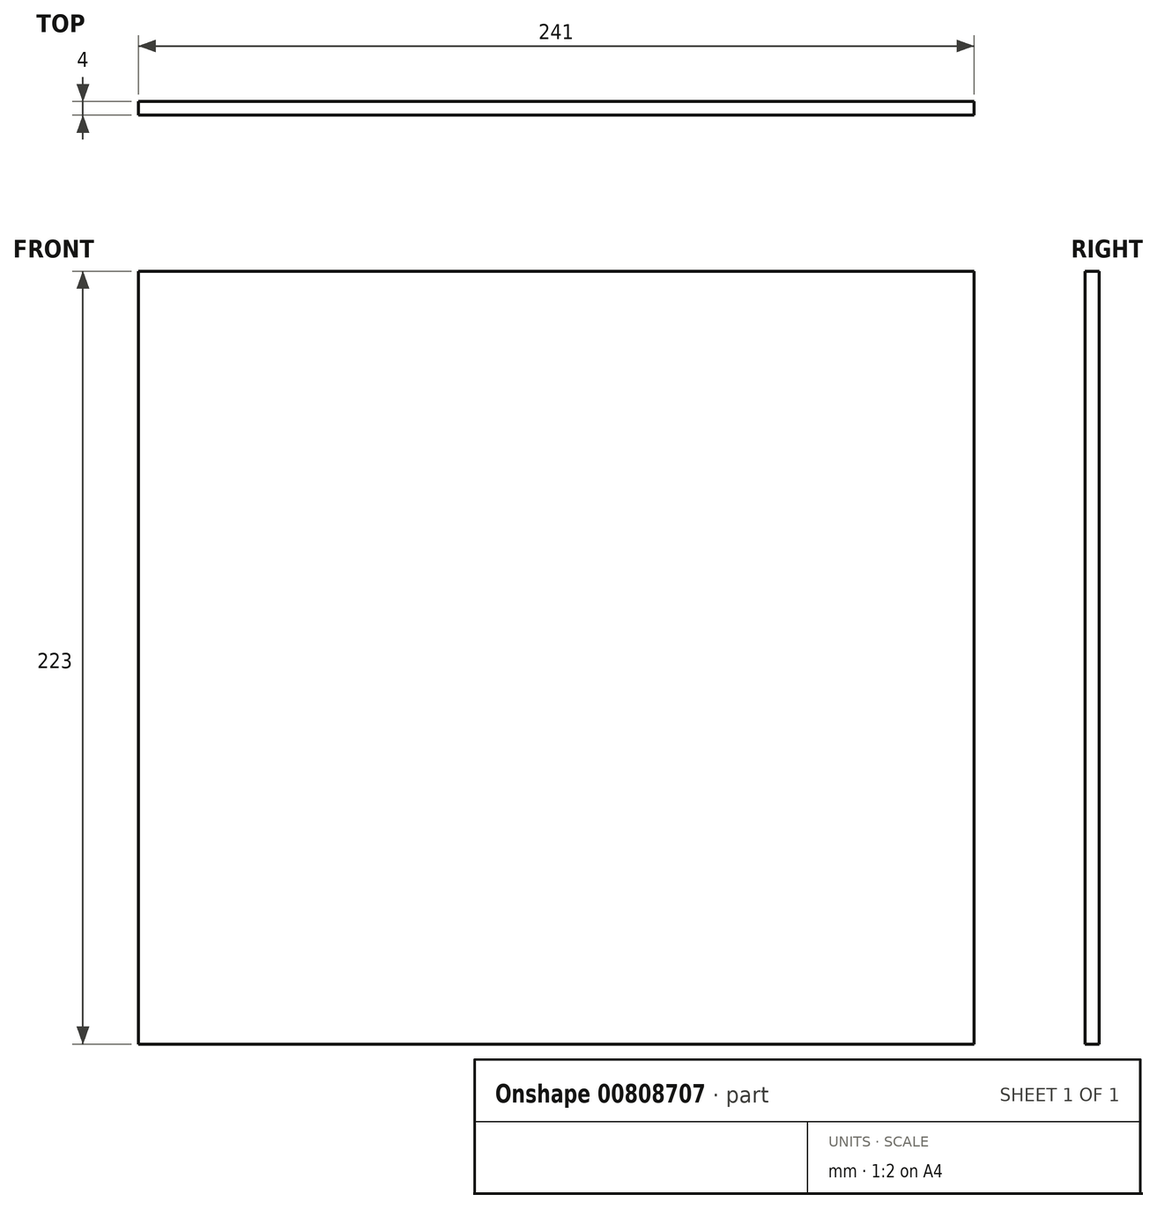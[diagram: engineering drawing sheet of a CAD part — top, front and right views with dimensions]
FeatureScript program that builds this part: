
annotation { "Feature Type Name" : "Feature", "Feature Type Description" : "" }
export const myFeature = defineFeature(function(context is Context, id is Id, definition is map)
    precondition{}
    {
        {
            var Q0;
            Q0=qCreatedBy(makeId("Front.planeOp"),FACE);
            var sketch = newSketch(context, id + "F0", { "sketchPlane" : qUnion([Q0])});
            skLineSegment(sketch, "E0.bottom", {"start": v(0, 0) * mm, "end": v(241, 0) * mm});
            skLineSegment(sketch, "E0.top", {"start": v(0, 223) * mm, "end": v(241, 223) * mm});
            skLineSegment(sketch, "E0.left", {"start": v(0, 0) * mm, "end": v(0, 223) * mm});
            skLineSegment(sketch, "E0.right", {"start": v(241, 0) * mm, "end": v(241, 223) * mm});
            skSolve(sketch);
        }
        {
            var Q0;
            Q0=makeQuery(id+"F0.imprint","IMPRINT",FACE,{"disambiguationData":[TD([[makeQuery(id+"F0.imprint","IMPRINT",EDGE,{"derivedFrom":sQuery(id+"F0.wireOp",EDGE,"E0.bottom")}),1.0]])]});
            var Q1;
            Q1 = qSketchRegion(id + "FO1Ut4vTHhWNYz2_0", true);
            extrude(context, id + "F1", {"entities" : qUnion([Q0, Q1]), "depth" : 4 * mm, "offsetDistance" : 25 * mm});
        }
    });
